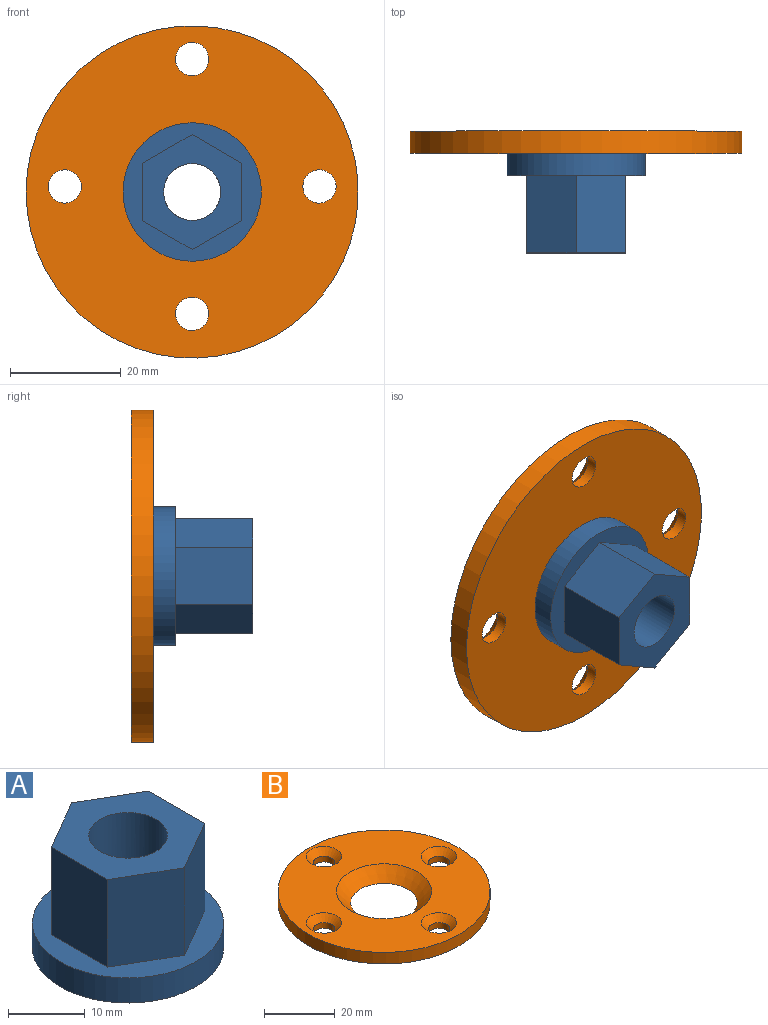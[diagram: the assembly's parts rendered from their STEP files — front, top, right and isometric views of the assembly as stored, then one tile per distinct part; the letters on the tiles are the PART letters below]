
ASSEMBLY  parts=2 mates=2
PART A: 11 faces, bbox 25x25x18 mm
  f0: plane 25x25mm, normal (0,0,1), area 210.3mm2, adj f1,f3,f4,f5,f6,f7,f8
  f1: cylinder r=12.5mm len=25mm, axis (0,0,1), area 314.2mm2, adj f0,f2
  f2: plane 25x25mm, normal (0,0,-1), area 407.6mm2, adj f1,f10
  f3: plane 14x9mm, normal (0.5,0.87,0), area 145.5mm2, adj f0,f4,f8,f9
  f4: plane 14x9mm, normal (-0.5,0.87,0), area 145.5mm2, adj f0,f3,f5,f9
  f5: plane 14x10.39mm, normal (-1,0,0), area 145.5mm2, adj f0,f4,f6,f9
  f6: plane 14x9mm, normal (-0.5,-0.87,0), area 145.5mm2, adj f0,f5,f7,f9
  f7: plane 14x9mm, normal (0.5,-0.87,0), area 145.5mm2, adj f0,f6,f8,f9
  f8: plane 14x10.39mm, normal (1,0,0), area 145.5mm2, adj f0,f3,f7,f9
  f9: plane 20.78x18mm, normal (0,0,1), area 197.3mm2, adj f3,f4,f5,f6,f7,f8,f10
  f10: cylinder r=5.15mm len=18mm, axis (0,0,-1), area 582.5mm2, adj f2,f9
PART B: 12 faces, bbox 60x60x4 mm
  f0: cylinder r=30mm len=60mm, axis (0,0,1), area 754mm2, adj f1,f2
  f1: plane 60x60mm, normal (0,0,-1), area 2434.4mm2, adj f0,f3,f4,f6,f8,f10
  f2: plane 60x60mm, normal (0,0,1), area 1945.8mm2, adj f0,f3,f5,f7,f9,f11
  f3: cone r=6.6mm half-angle=45deg, axis (0,0,1), area 406.6mm2, adj f1,f2
  f4: cylinder r=3mm len=6mm, axis (0,0,1), area 37.7mm2, adj f1,f5
  f5: cone r=3mm half-angle=45deg, axis (0,0,1), area 71.1mm2, adj f2,f4
  f6: cylinder r=3mm len=6mm, axis (0,0,1), area 37.7mm2, adj f1,f7
  f7: cone r=3mm half-angle=45deg, axis (0,0,1), area 71.1mm2, adj f2,f6
  f8: cylinder r=3mm len=6mm, axis (0,0,1), area 37.7mm2, adj f1,f9
  f9: cone r=3mm half-angle=45deg, axis (0,0,1), area 71.1mm2, adj f2,f8
  f10: cylinder r=3mm len=6mm, axis (0,0,1), area 37.7mm2, adj f1,f11
  f11: cone r=3mm half-angle=45deg, axis (0,0,1), area 71.1mm2, adj f2,f10
PLACE A rot(axis=(1,0,0),90deg) t=(0,-8,0)mm
PLACE B rot(axis=(0,0.71,0.71),180deg) t=(0,0,0)mm fixed
MATE cylindrical B.f0 <-> A.f1  axis (0,1,0) through (0,-2,0)mm
MATE planar B.f1 <-> A.f1  axis (0,-1,0) through (0,-4,-0.05)mm
